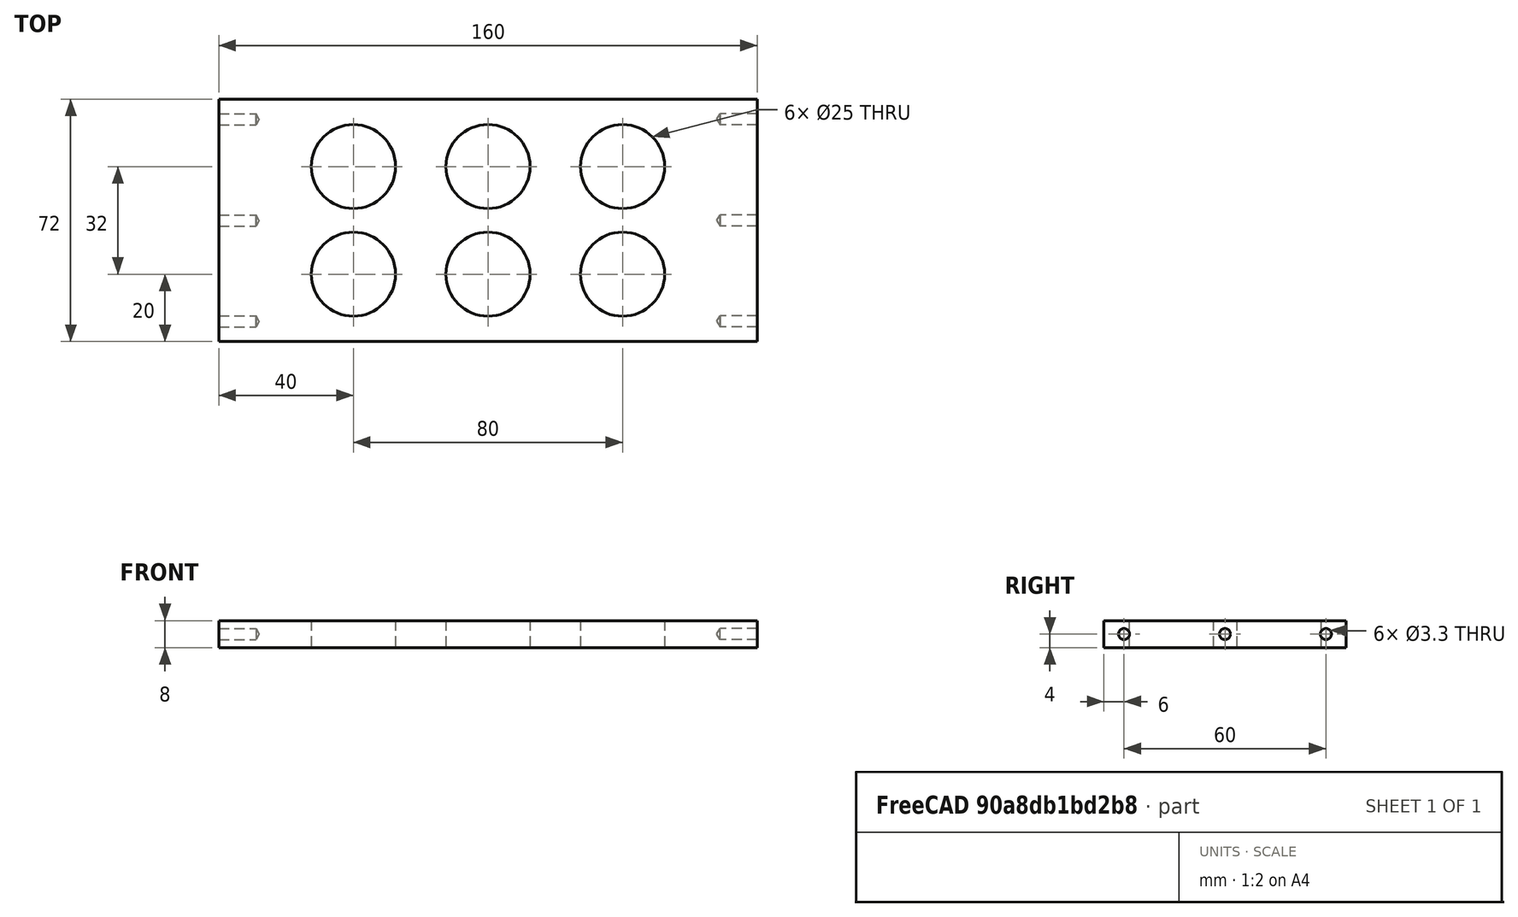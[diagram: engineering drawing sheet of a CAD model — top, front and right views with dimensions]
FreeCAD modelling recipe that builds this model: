
FCSTD DOCUMENT  (FreeCAD 0.17R13522 (Git))
Label: Boden
License: All rights reserved
LicenseURL: http://en.wikipedia.org/wiki/All_rights_reserved
objects: TechDraw::DrawViewDimension×14, Sketcher::SketchObject×3, PartDesign::Hole×3, TechDraw::DrawProjGroupItem×3, Part::Box×1, PartDesign::FeatureBase×1, TechDraw::DrawSVGTemplate×1, TechDraw::DrawViewAnnotation×1, PartDesign::Body×1, TechDraw::DrawProjGroup×1, TechDraw::DrawPage×1
note: 12 computed .brp shape members not serialized (recipe doc carries the construction recipe); baked Part::Feature solids carry a one-line shape summary decoded from their .brp

FEATURE [Part::Box] Box  label="Würfel"
  AttacherType = Attacher::AttachEngine3D
  Height = 8
  Length = 160
  Width = 72
FEATURE [PartDesign::FeatureBase] BaseFeature
  BaseFeature = -> Box
FEATURE [Sketcher::SketchObject] Sketch
  MapMode = 5
  Placement = pos=(0,0,0) rot=(0.57735,-0.57735,-0.57735;2.0944rad)
  Support = -> [BaseFeature]
  sketch-geometry (3):
    g0: Circle CenterX=-66 CenterY=4 CenterZ=0 NormalX=0 NormalY=0 NormalZ=1 AngleXU=0 Radius=2
    g1: Circle CenterX=-36 CenterY=4 CenterZ=0 NormalX=0 NormalY=0 NormalZ=1 AngleXU=0 Radius=2
    g2: Circle CenterX=-6 CenterY=4 CenterZ=0 NormalX=0 NormalY=0 NormalZ=1 AngleXU=0 Radius=2
  constraints (9):
    c: Radius(g2) = 2
    c: Radius(g1) = 2
    c: Radius(g0) = 2
    c: DistanceY(g-1,g2) = 4
    c: Horizontal(g0,g1)
    c: Horizontal(g1,g2)
    c: DistanceX(g2,g-1) = 6
    c: DistanceX(g1,g-1) = 36
    c: DistanceX(g0,g-1) = 66
FEATURE [PartDesign::Hole] Hole
  BaseFeature = -> BaseFeature
  Depth = 12
  DepthType = 0
  Diameter = 3.3
  DrillPoint = 1
  DrillPointAngle = 118
  HoleCutCountersinkAngle = 90
  HoleCutDepth = 0
  HoleCutDiameter = 4
  HoleCutType = 0
  ModelActualThread = false
  Profile = -> Sketch
  Tapered = false
  TaperedAngle = 90
  ThreadAngle = 60
  ThreadClass = 0
  ThreadCutOffInner = 0.0757772
  ThreadCutOffOuter = 0.151554
  ThreadDirection = 1
  ThreadFit = 0
  ThreadPitch = 0.7
  ThreadSize = 5
  ThreadType = 1
  Threaded = true
FEATURE [Sketcher::SketchObject] Sketch001
  MapMode = 5
  Placement = pos=(160,0,0) rot=(0.57735,0.57735,0.57735;2.0944rad)
  Support = -> [Hole]
  sketch-geometry (3):
    g0: Circle CenterX=6 CenterY=4 CenterZ=0 NormalX=0 NormalY=0 NormalZ=1 AngleXU=0 Radius=2
    g1: Circle CenterX=36 CenterY=4 CenterZ=0 NormalX=0 NormalY=0 NormalZ=1 AngleXU=0 Radius=2
    g2: Circle CenterX=66 CenterY=4 CenterZ=0 NormalX=0 NormalY=0 NormalZ=1 AngleXU=0 Radius=2
  constraints (9):
    c: Radius(g0) = 2
    c: Radius(g1) = 2
    c: Radius(g2) = 2
    c: Horizontal(g0,g1)
    c: Horizontal(g1,g2)
    c: DistanceY(g-1,g0) = 4
    c: DistanceX(g-1,g0) = 6
    c: DistanceX(g-1,g1) = 36
    c: DistanceX(g-1,g2) = 66
FEATURE [PartDesign::Hole] Hole001
  BaseFeature = -> Hole
  Depth = 12
  DepthType = 0
  Diameter = 3.3
  DrillPoint = 1
  DrillPointAngle = 118
  HoleCutCountersinkAngle = 90
  HoleCutDepth = 0
  HoleCutDiameter = 4
  HoleCutType = 0
  ModelActualThread = false
  Profile = -> Sketch001
  Tapered = false
  TaperedAngle = 90
  ThreadAngle = 60
  ThreadClass = 0
  ThreadCutOffInner = 0.0757772
  ThreadCutOffOuter = 0.151554
  ThreadDirection = 1
  ThreadFit = 0
  ThreadPitch = 0.7
  ThreadSize = 5
  ThreadType = 1
  Threaded = true
FEATURE [TechDraw::DrawSVGTemplate] Template
  EditableTexts = Designed_by_Name=Christian; FC-Date=25.05.2018; FC-SC=1/1; FC-SH=1/1; FC-Title=Bodenplatte
  Height = 210
  Orientation = 1
  Width = 297
FEATURE [TechDraw::DrawViewAnnotation] Annotation
  Font = osifont
  LineSpace = 80
  LockPosition = false
  MaxWidth = -1
  Rotation = 0
  ScaleType = 0
  Text = Bohrungen sind eig. | M4 Gewinde |  Tiefe ca 12mm 
  TextSize = 8
  TextStyle = 0
  X = 89.6247
  Y = 40.5269
FEATURE [Sketcher::SketchObject] Sketch002
  MapMode = 5
  Placement = pos=(0,0,8) rot=(0,0,1;0rad)
  Support = -> [Hole001]
  sketch-geometry (6):
    g0: Circle CenterX=40 CenterY=52 CenterZ=0 NormalX=0 NormalY=0 NormalZ=1 AngleXU=0 Radius=12.5
    g1: Circle CenterX=40 CenterY=20 CenterZ=0 NormalX=0 NormalY=0 NormalZ=1 AngleXU=0 Radius=12.5
    g2: Circle CenterX=120 CenterY=52 CenterZ=0 NormalX=0 NormalY=0 NormalZ=1 AngleXU=0 Radius=12.5
    g3: Circle CenterX=120 CenterY=20 CenterZ=0 NormalX=0 NormalY=0 NormalZ=1 AngleXU=0 Radius=12.5
    g4: Circle CenterX=80 CenterY=52 CenterZ=0 NormalX=0 NormalY=0 NormalZ=1 AngleXU=0 Radius=12.5
    g5: Circle CenterX=80 CenterY=20 CenterZ=0 NormalX=0 NormalY=0 NormalZ=1 AngleXU=0 Radius=12.5
  constraints (18):
    c: Radius(g0) = 12.5
    c: Radius(g1) = 12.5
    c: Radius(g2) = 12.5
    c: Radius(g3) = 12.5
    c: Vertical(g1,g0)
    c: Vertical(g2,g3)
    c: Horizontal(g0,g2)
    c: Horizontal(g1,g3)
    c: DistanceY(g-1,g1) = 20
    c: DistanceY(g-1,g0) = 52
    c: DistanceX(g-1,g1) = 40
    c: DistanceX(g-1,g3) = 120
    c: Radius(g5) = 12.5
    c: Radius(g4) = 12.5
    c: Horizontal(g4,g0)
    c: Vertical(g4,g5)
    c: Horizontal(g5,g1)
    c: DistanceX(g-1,g5) = 80
FEATURE [PartDesign::Hole] Hole002
  BaseFeature = -> Hole001
  Depth = 25
  DepthType = 1
  Diameter = 25
  DrillPoint = 1
  DrillPointAngle = 118
  HoleCutCountersinkAngle = 90
  HoleCutDepth = 0
  HoleCutDiameter = 0
  HoleCutType = 0
  ModelActualThread = false
  Profile = -> Sketch002
  Tapered = false
  TaperedAngle = 90
  ThreadAngle = 0
  ThreadClass = 0
  ThreadCutOffInner = 0
  ThreadCutOffOuter = 0
  ThreadDirection = 0
  ThreadFit = 0
  ThreadPitch = 0
  ThreadSize = 0
  ThreadType = 0
  Threaded = false
FEATURE [PartDesign::Body] Body
  BaseFeature = -> Box
  Group = -> [BaseFeature,Sketch,Hole,Sketch001,Hole001,Sketch002,Hole002]
  Origin = -> Origin
  Tip = -> Hole002
FEATURE [TechDraw::DrawProjGroupItem] ProjItem  label="Front"
  CoarseView = false
  Direction = (1,0,0)
  Focus = 100
  HardHidden = false
  IsoCount = 0
  IsoHidden = false
  IsoVisible = false
  LockPosition = false
  Perspective = false
  Rotation = 0
  RotationVector = (0,0,-1)
  ScaleType = 0
  SeamHidden = false
  SeamVisible = false
  SmoothHidden = false
  SmoothVisible = false
  Source = -> [Body]
  Type = 0
  X = -125.5
  Y = 0
FEATURE [TechDraw::DrawProjGroupItem] ProjItem001  label="Left"
  CoarseView = false
  Direction = (0,0,1)
  Focus = 100
  HardHidden = false
  IsoCount = 0
  IsoHidden = false
  IsoVisible = false
  LockPosition = true
  Perspective = false
  Rotation = 0
  RotationVector = (1,0,0)
  ScaleType = 0
  SeamHidden = false
  SeamVisible = false
  SmoothHidden = false
  SmoothVisible = false
  Source = -> [Body]
  Type = 1
  X = 144.552
  Y = 0
FEATURE [TechDraw::DrawProjGroupItem] ProjItem002  label="Rear"
  CoarseView = false
  Direction = (-1,0,0)
  Focus = 100
  HardHidden = false
  IsoCount = 0
  IsoHidden = false
  IsoVisible = false
  LockPosition = true
  Perspective = false
  Rotation = 0
  RotationVector = (0,0,1)
  ScaleType = 0
  SeamHidden = false
  SeamVisible = false
  SmoothHidden = false
  SmoothVisible = false
  Source = -> [Body]
  Type = 3
  X = 255.783
  Y = 0
FEATURE [TechDraw::DrawProjGroup] ProjGroup
  Anchor = -> ProjItem
  AutoDistribute = true
  CubeDirs = (6) [(-6.12323e-17,-1,-6.12323e-17),(1,-6.12323e-17,0),(-3.7494e-33,-6.12323e-17,1),(-1,6.12323e-17,0),(3.7494e-33,6.12323e-17,-1),(6.12323e-17,1,6.12323e-17)]
  CubeRotations = (6) [(1.22465e-16,-6.12323e-17,-1),(1.22465e-16,-6.12323e-17,-1),(1,6.12323e-17,0),(-1.22465e-16,6.12323e-17,1),(-1,-6.12323e-17,0),(1.22465e-16,-6.12323e-17,-1)]
  LockPosition = false
  ProjectionType = 0
  Rotation = 0
  ScaleType = 0
  Source = -> [Body]
  Views = -> [ProjItem,ProjItem001,ProjItem002]
  X = 26.1415
  Y = 147.421
  spacingX = 15
  spacingY = 15
FEATURE [TechDraw::DrawViewDimension] Dimension
  FormatSpec = %.2f
  LockPosition = false
  MeasureType = 1
  References2D = -> [ProjItem]
  Rotation = 0
  ScaleType = 0
  Type = 1
  X = 17.1252
  Y = -73.4698
FEATURE [TechDraw::DrawViewDimension] Dimension001
  FormatSpec = %.2f
  LockPosition = false
  MeasureType = 1
  References2D = -> [ProjItem]
  Rotation = 0
  ScaleType = 0
  Type = 2
  X = 12.7341
  Y = -50.9364
FEATURE [TechDraw::DrawViewDimension] Dimension002
  FormatSpec = %.2f
  LockPosition = false
  MeasureType = 1
  References2D = -> [ProjItem]
  Rotation = 0
  ScaleType = 0
  Type = 2
  X = 23.2341
  Y = -21.0001
FEATURE [TechDraw::DrawViewDimension] Dimension003
  FormatSpec = %.2f
  LockPosition = false
  MeasureType = 1
  References2D = -> [ProjItem]
  Rotation = 0
  ScaleType = 0
  Type = 2
  X = 30.765
  Y = -20.9642
FEATURE [TechDraw::DrawViewDimension] Dimension004
  FormatSpec = %.2f
  LockPosition = false
  MeasureType = 1
  References2D = -> [ProjItem]
  Rotation = 0
  ScaleType = 0
  Type = 5
  X = 31.0533
  Y = 44.0108
FEATURE [TechDraw::DrawViewDimension] Dimension005
  FormatSpec = %.2f
  LockPosition = false
  MeasureType = 1
  References2D = -> [ProjItem001]
  Rotation = 0
  ScaleType = 0
  Type = 1
  X = 1.7178
  Y = -72.5365
FEATURE [TechDraw::DrawViewDimension] Dimension006
  FormatSpec = %.2f
  LockPosition = false
  MeasureType = 1
  References2D = -> [ProjItem]
  Rotation = 0
  ScaleType = 0
  Type = 2
  X = 38.7649
  Y = -21.4382
FEATURE [TechDraw::DrawViewDimension] Dimension007
  FormatSpec = %.2f
  LockPosition = false
  MeasureType = 1
  References2D = -> [ProjItem]
  Rotation = 0
  ScaleType = 0
  Type = 1
  X = 17.3349
  Y = -65.8727
FEATURE [TechDraw::DrawViewDimension] Dimension008
  FormatSpec = %.2f
  LockPosition = false
  MeasureType = 1
  References2D = -> [ProjItem001]
  Rotation = 0
  ScaleType = 0
  Type = 5
  X = 7.78914
  Y = 43.8417
FEATURE [TechDraw::DrawViewDimension] Dimension009
  FormatSpec = %.2f
  LockPosition = false
  MeasureType = 1
  References2D = -> [ProjItem001]
  Rotation = 0
  ScaleType = 0
  Type = 1
  X = -57.7777
  Y = -42.6629
FEATURE [TechDraw::DrawViewDimension] Dimension010
  FormatSpec = %.2f
  LockPosition = false
  MeasureType = 1
  References2D = -> [ProjItem001]
  Rotation = 0
  ScaleType = 0
  Type = 1
  X = -32.9114
  Y = -52.4144
FEATURE [TechDraw::DrawViewDimension] Dimension011
  FormatSpec = %.2f
  LockPosition = false
  MeasureType = 1
  References2D = -> [ProjItem001]
  Rotation = 0
  ScaleType = 0
  Type = 1
  X = -8.53257
  Y = -62.1659
FEATURE [TechDraw::DrawViewDimension] Dimension012
  FormatSpec = %.2f
  LockPosition = false
  MeasureType = 1
  References2D = -> [ProjItem001]
  Rotation = 0
  ScaleType = 0
  Type = 2
  X = 85.5695
  Y = -25.8415
FEATURE [TechDraw::DrawViewDimension] Dimension013
  FormatSpec = %.2f
  LockPosition = false
  MeasureType = 1
  References2D = -> [ProjItem001]
  Rotation = 0
  ScaleType = 0
  Type = 2
  X = 92.8832
  Y = -2.68167
FEATURE [TechDraw::DrawPage] Page
  KeepUpdated = true
  ProjectionType = 0
  Template = -> Template
  Views = -> [ProjGroup,Dimension,Dimension001,Dimension002,Dimension003,Dimension004,Dimension005,Dimension006,Annotation,Dimension007,Dimension008,Dimension009,Dimension010,Dimension011,Dimension012,Dimension013]
